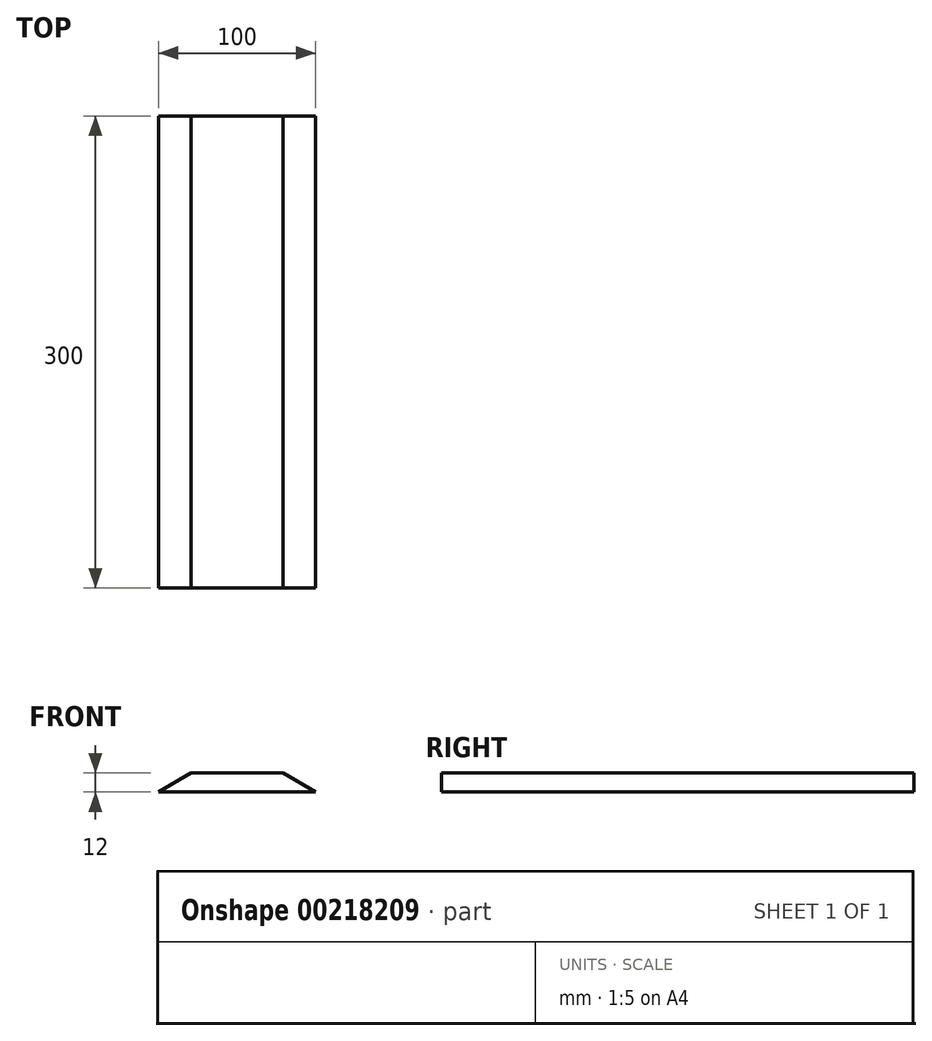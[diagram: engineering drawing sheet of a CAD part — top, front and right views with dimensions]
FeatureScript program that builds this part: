
annotation { "Feature Type Name" : "Feature", "Feature Type Description" : "" }
export const myFeature = defineFeature(function(context is Context, id is Id, definition is map)
    precondition{}
    {
        {
            var Q0;
            Q0=qCreatedBy(makeId("Top.planeOp"),FACE);
            var sketch = newSketch(context, id + "F0", { "sketchPlane" : qUnion([Q0])});
            skLineSegment(sketch, "E0.bottom", {"start": v(-50, 150) * mm, "end": v(50, 150) * mm});
            skLineSegment(sketch, "E0.top", {"start": v(-50, -150) * mm, "end": v(50, -150) * mm});
            skLineSegment(sketch, "E0.left", {"start": v(-50, 150) * mm, "end": v(-50, -150) * mm});
            skLineSegment(sketch, "E0.right", {"start": v(50, 150) * mm, "end": v(50, -150) * mm});
            skSolve(sketch);
        }
        {
            var Q0;
            Q0=makeQuery(id+"F0.imprint","IMPRINT",FACE,{"disambiguationData":[TD([[makeQuery(id+"F0.imprint","IMPRINT",EDGE,{"derivedFrom":sQuery(id+"F0.wireOp",EDGE,"E0.bottom")}),-1.0]])]});
            extrude(context, id + "F1", {"entities" : qUnion([Q0]), "depth" : 12 * mm, "offsetDistance" : 25 * mm});
        }
        {
            var Q0;
            Q0=makeQuery(id+"F1.opExtrude","SWEPT_FACE",FACE,{"disambiguationData":[OSD([sQuery(id+"F0.wireOp",EDGE,"E0.top")])]});
            var sketch = newSketch(context, id + "F2", { "sketchPlane" : qUnion([Q0])});
            skLineSegment(sketch, "E1", {"start": v(50, 12) * mm, "end": v(29.22, 12) * mm});
            skLineSegment(sketch, "E2", {"start": v(29.22, 12) * mm, "end": v(50, 0) * mm});
            skLineSegment(sketch, "E3", {"start": v(50, 0) * mm, "end": v(50, 12) * mm});
            skLineSegment(sketch, "E4", {"start": v(-50, 12) * mm, "end": v(-50, 0) * mm});
            skLineSegment(sketch, "E5", {"start": v(-50, 0) * mm, "end": v(-29.22, 12) * mm});
            skLineSegment(sketch, "E6", {"start": v(-29.22, 12) * mm, "end": v(-50, 12) * mm});
            skSolve(sketch);
        }
        {
            var Q0;
            Q0 = qSketchRegion(id + "F2", true);
            extrude(context, id + "F3", {"entities" : qUnion([Q0]), "operationType" : NewBodyOperationType.REMOVE, "endBound" : BoundingType.THROUGH_ALL, "oppositeDirection" : true, "depth" : 25 * mm, "offsetDistance" : 25 * mm});
        }
    });
